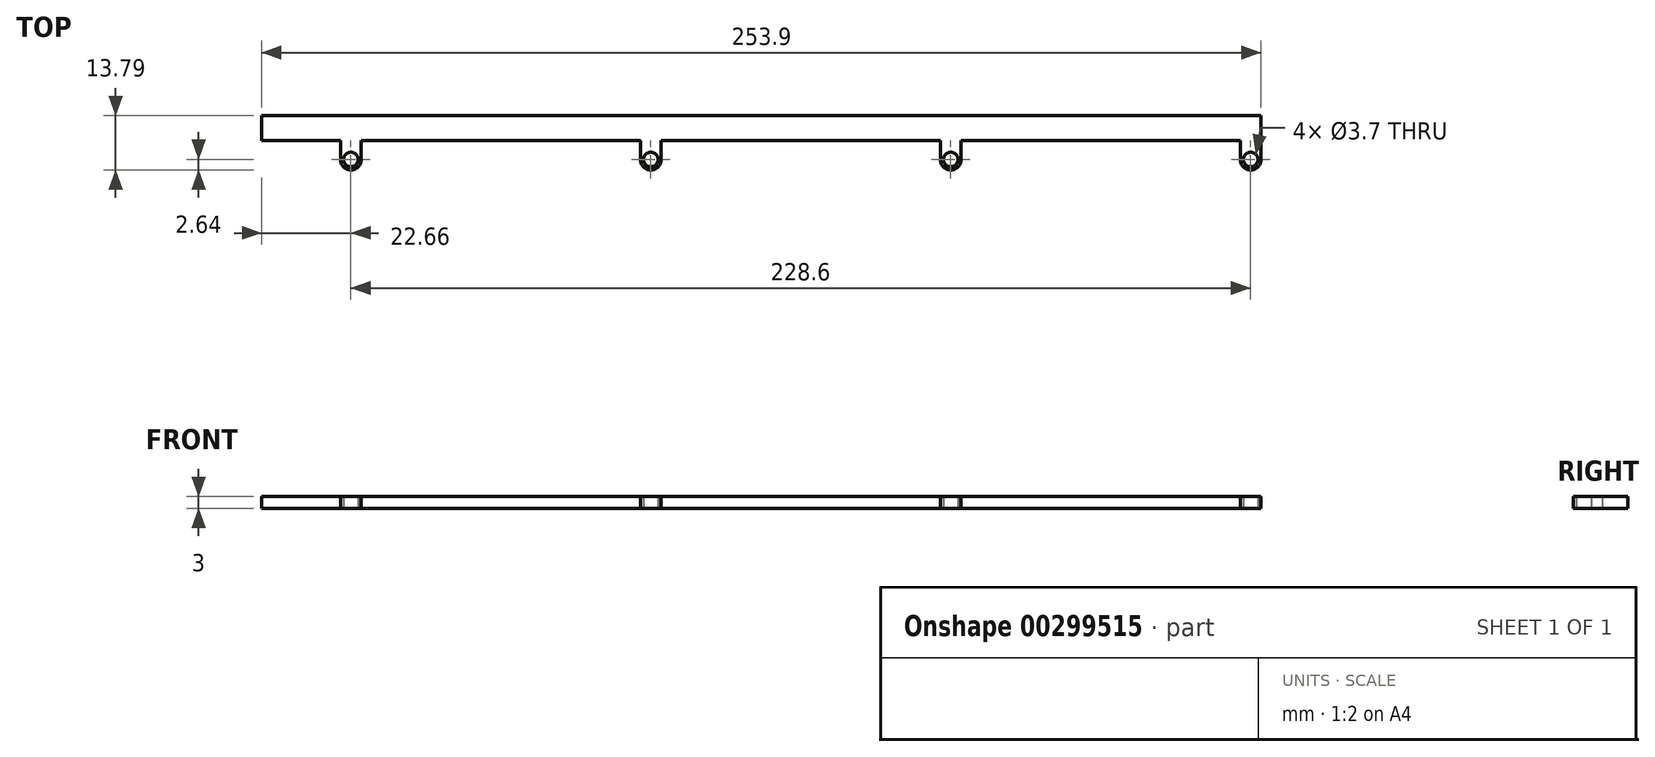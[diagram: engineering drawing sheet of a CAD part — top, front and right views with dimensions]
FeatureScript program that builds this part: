
annotation { "Feature Type Name" : "Feature", "Feature Type Description" : "" }
export const myFeature = defineFeature(function(context is Context, id is Id, definition is map)
    precondition{}
    {
        {
            var Q0;
            Q0=qCreatedBy(makeId("Top.planeOp"),FACE);
            var sketch = newSketch(context, id + "F0", { "sketchPlane" : qUnion([Q0])});
            skLineSegment(sketch, "E0.bottom", {"start": v(126.95, 3.2) * mm, "end": v(-126.95, 3.2) * mm});
            skLineSegment(sketch, "E0.top", {"start": v(126.95, -3.2) * mm, "end": v(-126.95, -3.2) * mm});
            skLineSegment(sketch, "E0.left", {"start": v(126.95, 3.2) * mm, "end": v(126.95, -3.2) * mm});
            skLineSegment(sketch, "E0.right", {"start": v(-126.95, 3.2) * mm, "end": v(-126.95, -3.2) * mm});
            skPoint(sketch, "E0.middle", {"position": v(0, 0) * mm});
            skSolve(sketch);
        }
        {
            var Q0;
            Q0=makeQuery(id+"F0.imprint","IMPRINT",FACE,{"disambiguationData":[TD([[makeQuery(id+"F0.imprint","IMPRINT",EDGE,{"derivedFrom":sQuery(id+"F0.wireOp",EDGE,"E0.bottom")}),1.0]])]});
            extrude(context, id + "F1", {"entities" : qUnion([Q0]), "depth" : 3 * mm});
        }
        {
            var Q0;
            Q0=qCreatedBy(makeId("Top.planeOp"),FACE);
            var sketch = newSketch(context, id + "F2", { "sketchPlane" : qUnion([Q0])});
            skLineSegment(sketch, "E1.bottom", {"start": v(126.95, -3.2) * mm, "end": v(121.67, -3.2) * mm});
            skLineSegment(sketch, "E1.top", {"start": v(126.95, -10.59) * mm, "end": v(121.67, -10.59) * mm});
            skLineSegment(sketch, "E1.left", {"start": v(126.95, -3.2) * mm, "end": v(126.95, -10.59) * mm});
            skLineSegment(sketch, "E1.right", {"start": v(121.67, -3.2) * mm, "end": v(121.67, -10.59) * mm});
            skCircle(sketch, "E2", {"center": v(124.3, -7.95) * mm, "radius": 1.85 * mm});
            skLineSegment(sketch, "E3", {"start": v(124.3, -7.95) * mm, "end": v(124.3, -10.59) * mm});
            skLineSegment(sketch, "E4", {"start": v(124.3, -7.95) * mm, "end": v(121.67, -7.95) * mm});
            skLineSegment(sketch, "E5.bottom", {"start": v(50.75, -3.2) * mm, "end": v(45.47, -3.2) * mm});
            skLineSegment(sketch, "E5.top", {"start": v(50.75, -10.59) * mm, "end": v(45.47, -10.59) * mm});
            skLineSegment(sketch, "E5.left", {"start": v(50.75, -3.2) * mm, "end": v(50.75, -10.59) * mm});
            skLineSegment(sketch, "E5.right", {"start": v(45.47, -3.2) * mm, "end": v(45.47, -10.6) * mm});
            skCircle(sketch, "E6", {"center": v(48.1, -7.95) * mm, "radius": 1.85 * mm});
            skPoint(sketch, "E6.centerSnap0", {"position": v(48.1, -10.6) * mm});
            skLineSegment(sketch, "E7", {"start": v(48.1, -7.95) * mm, "end": v(45.47, -7.95) * mm});
            skPoint(sketch, "E7.endSnap0", {"position": v(45.47, -6.9) * mm});
            skLineSegment(sketch, "E8.bottom", {"start": v(-30.73, -3.2) * mm, "end": v(-25.45, -3.2) * mm});
            skLineSegment(sketch, "E8.top", {"start": v(-30.73, -10.59) * mm, "end": v(-25.45, -10.59) * mm});
            skLineSegment(sketch, "E8.left", {"start": v(-30.73, -3.2) * mm, "end": v(-30.73, -10.59) * mm});
            skLineSegment(sketch, "E8.right", {"start": v(-25.45, -3.2) * mm, "end": v(-25.45, -10.59) * mm});
            skLineSegment(sketch, "E9.bottom", {"start": v(-106.93, -3.2) * mm, "end": v(-101.65, -3.2) * mm});
            skLineSegment(sketch, "E9.top", {"start": v(-106.93, -10.59) * mm, "end": v(-101.65, -10.59) * mm});
            skLineSegment(sketch, "E9.left", {"start": v(-106.93, -3.2) * mm, "end": v(-106.93, -10.59) * mm});
            skLineSegment(sketch, "E9.right", {"start": v(-101.65, -3.2) * mm, "end": v(-101.65, -10.59) * mm});
            skCircle(sketch, "E10", {"center": v(-28.1, -7.95) * mm, "radius": 1.85 * mm});
            skCircle(sketch, "E11", {"center": v(-104.3, -7.95) * mm, "radius": 1.85 * mm});
            skLineSegment(sketch, "E12", {"start": v(-104.3, -7.95) * mm, "end": v(-106.93, -7.95) * mm});
            skLineSegment(sketch, "E13", {"start": v(-28.1, -7.95) * mm, "end": v(-30.73, -7.95) * mm});
            skSolve(sketch);
        }
        {
            var Q0;
            {var subQ1=sQuery(id+"F2.wireOp",EDGE,"E1.bottom");Q0=makeQuery(id+"F2.imprint","IMPRINT",FACE,{"disambiguationData":[TD([[makeQuery(id+"F2.imprint","IMPRINT",EDGE,{"derivedFrom":subQ1}),1.0]])]});}
            var Q1;
            {var subQ1=sQuery(id+"F2.wireOp",EDGE,"E1.top");var subQ7=sQuery(id+"F2.wireOp",EDGE,"E1.right");var subQ8=makeQuery(id+"F2.imprint","INTERSECT",VERTEX,{"derivedFrom":[subQ1,subQ7]});Q1=makeQuery(id+"F2.imprint","IMPRINT",FACE,{"disambiguationData":[TD([[makeQuery(id+"F2.imprint","IMPRINT",EDGE,{"disambiguationData":[TD([[subQ8,1.0]])],"derivedFrom":subQ1}),-1.0]])]});}
            var Q2;
            {var subQ1=sQuery(id+"F2.wireOp",EDGE,"E5.bottom");Q2=makeQuery(id+"F2.imprint","IMPRINT",FACE,{"disambiguationData":[TD([[makeQuery(id+"F2.imprint","IMPRINT",EDGE,{"derivedFrom":subQ1}),1.0]])]});}
            var Q3;
            {var subQ3=sQuery(id+"F2.wireOp",EDGE,"E9.bottom");Q3=makeQuery(id+"F2.imprint","IMPRINT",FACE,{"disambiguationData":[TD([[makeQuery(id+"F2.imprint","IMPRINT",EDGE,{"derivedFrom":subQ3}),-1.0]])]});}
            var Q4;
            {var subQ3=sQuery(id+"F2.wireOp",EDGE,"E8.bottom");Q4=makeQuery(id+"F2.imprint","IMPRINT",FACE,{"disambiguationData":[TD([[makeQuery(id+"F2.imprint","IMPRINT",EDGE,{"derivedFrom":subQ3}),-1.0]])]});}
            extrude(context, id + "F3", {"entities" : qUnion([Q0, Q1, Q2, Q3, Q4]), "operationType" : NewBodyOperationType.ADD, "depth" : 3 * mm});
        }
        {
            var Q0;
            Q0=makeQuery(id+"F3.opExtrude","SWEPT_EDGE",EDGE,{"disambiguationData":[OSD([sQuery(id+"F2.wireOp",EDGE,"E5.top"),sQuery(id+"F2.wireOp",EDGE,"E5.right")])]});
            var Q1;
            Q1=makeQuery(id+"F3.opExtrude","SWEPT_EDGE",EDGE,{"disambiguationData":[OSD([sQuery(id+"F2.wireOp",EDGE,"E5.top"),sQuery(id+"F2.wireOp",EDGE,"E5.left")])]});
            var Q2;
            Q2=makeQuery(id+"F3.opExtrude","SWEPT_EDGE",EDGE,{"disambiguationData":[OSD([sQuery(id+"F2.wireOp",EDGE,"E1.top"),sQuery(id+"F2.wireOp",EDGE,"E1.right")])]});
            var Q3;
            Q3=makeQuery(id+"F3.opExtrude","SWEPT_EDGE",EDGE,{"disambiguationData":[OSD([sQuery(id+"F2.wireOp",EDGE,"E1.top"),sQuery(id+"F2.wireOp",EDGE,"E1.left")])]});
            var Q4;
            Q4=makeQuery(id+"F3.opExtrude","SWEPT_EDGE",EDGE,{"disambiguationData":[OSD([sQuery(id+"F2.wireOp",EDGE,"E8.top"),sQuery(id+"F2.wireOp",EDGE,"E8.left")])]});
            var Q5;
            Q5=makeQuery(id+"F3.opExtrude","SWEPT_EDGE",EDGE,{"disambiguationData":[OSD([sQuery(id+"F2.wireOp",EDGE,"E8.top"),sQuery(id+"F2.wireOp",EDGE,"E8.right")])]});
            var Q6;
            Q6=makeQuery(id+"F3.opExtrude","SWEPT_EDGE",EDGE,{"disambiguationData":[OSD([sQuery(id+"F2.wireOp",EDGE,"E9.top"),sQuery(id+"F2.wireOp",EDGE,"E9.left")])]});
            var Q7;
            Q7=makeQuery(id+"F3.opExtrude","SWEPT_EDGE",EDGE,{"disambiguationData":[OSD([sQuery(id+"F2.wireOp",EDGE,"E9.top"),sQuery(id+"F2.wireOp",EDGE,"E9.right")])]});
            fillet(context, id + "F4", {"entities" : qUnion([Q0, Q1, Q2, Q3, Q4, Q5, Q6, Q7]), "radius" : 2.64 * mm, "tangentPropagation" : true, "allowEdgeOverflow" : false});
        }
    });
